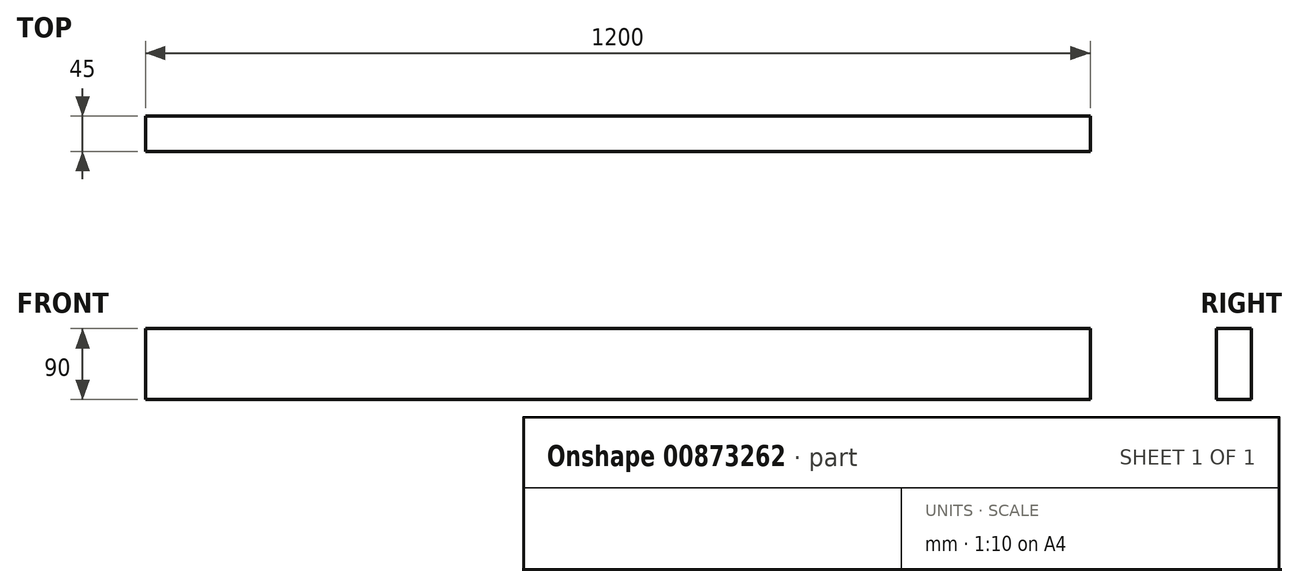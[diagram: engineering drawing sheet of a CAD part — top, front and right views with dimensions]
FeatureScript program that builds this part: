
annotation { "Feature Type Name" : "Feature", "Feature Type Description" : "" }
export const myFeature = defineFeature(function(context is Context, id is Id, definition is map)
    precondition{}
    {
        {
            var Q0;
            Q0=qCreatedBy(makeId("Front.planeOp"),FACE);
            var sketch = newSketch(context, id + "F0", { "sketchPlane" : qUnion([Q0])});
            skLineSegment(sketch, "E0.bottom", {"start": v(-600, 45) * mm, "end": v(600, 45) * mm});
            skLineSegment(sketch, "E0.top", {"start": v(-600, -45) * mm, "end": v(600, -45) * mm});
            skLineSegment(sketch, "E0.left", {"start": v(-600, 45) * mm, "end": v(-600, -45) * mm});
            skLineSegment(sketch, "E0.right", {"start": v(600, 45) * mm, "end": v(600, -45) * mm});
            skPoint(sketch, "E0.middle", {"position": v(0, 0) * mm});
            skSolve(sketch);
        }
        {
            var Q0;
            Q0 = qSketchRegion(id + "F0", true);
            extrude(context, id + "F1", {"entities" : qUnion([Q0]), "depth" : 45 * mm, "offsetDistance" : 25 * mm});
        }
    });
